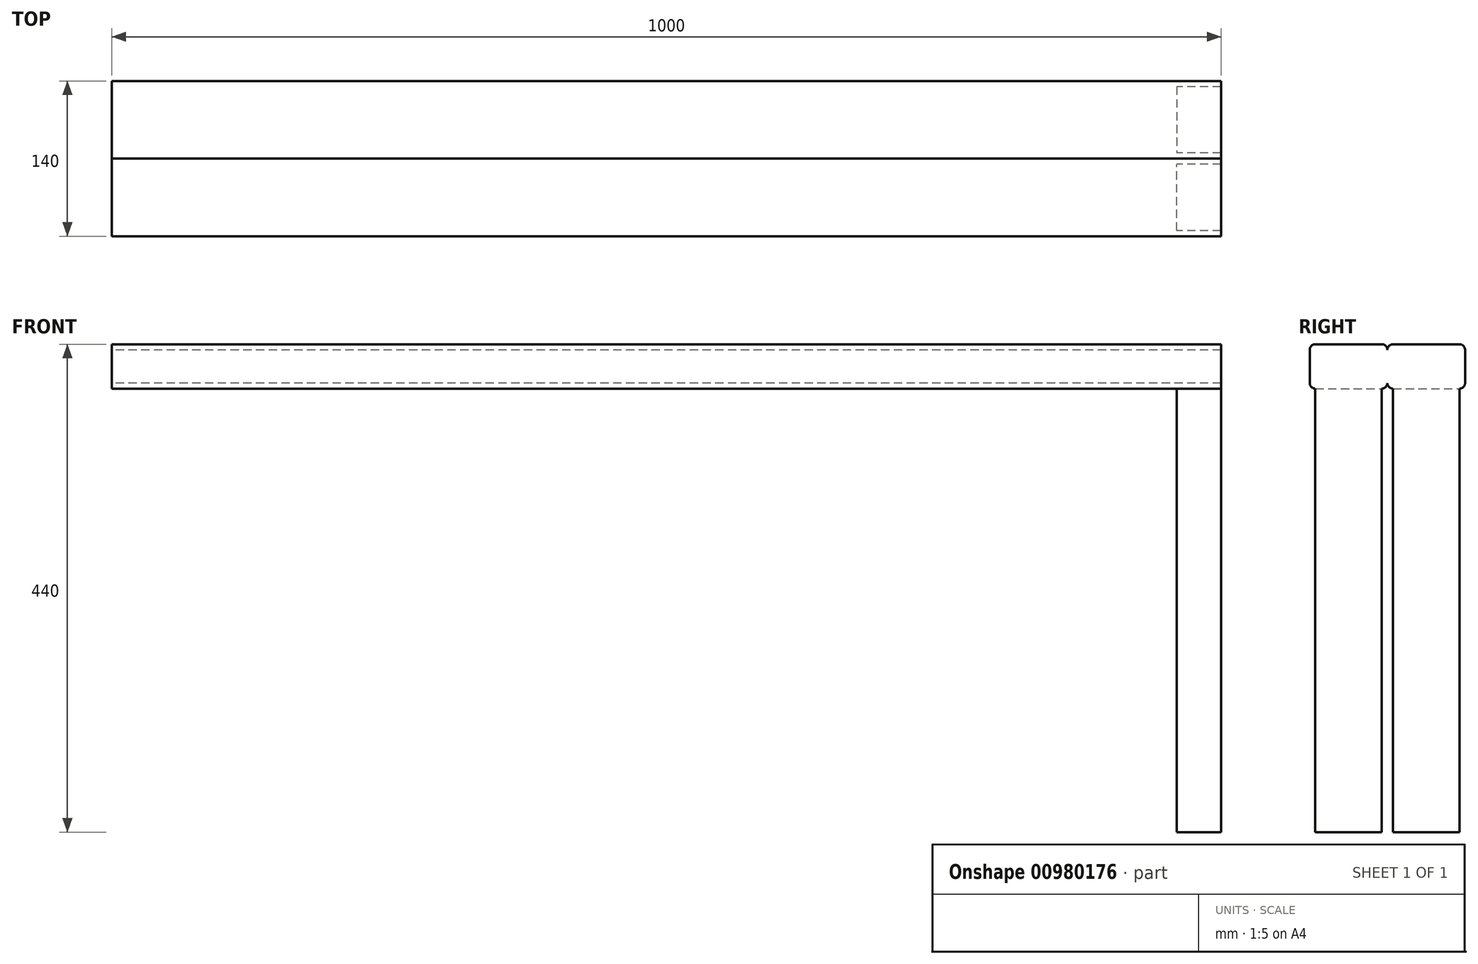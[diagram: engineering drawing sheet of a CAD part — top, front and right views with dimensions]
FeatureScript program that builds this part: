
annotation { "Feature Type Name" : "Feature", "Feature Type Description" : "" }
export const myFeature = defineFeature(function(context is Context, id is Id, definition is map)
    precondition{}
    {
        {
            var Q0;
            Q0=qCreatedBy(makeId("Right.planeOp"),FACE);
            var sketch = newSketch(context, id + "F0", { "sketchPlane" : qUnion([Q0])});
            skLineSegment(sketch, "E0.bottom", {"start": v(-5, 0) * mm, "end": v(-65, 0) * mm});
            skLineSegment(sketch, "E0.top", {"start": v(-5, 40) * mm, "end": v(-65, 40) * mm});
            skLineSegment(sketch, "E0.left", {"start": v(0, 5) * mm, "end": v(0, 35) * mm});
            skLineSegment(sketch, "E0.right", {"start": v(-70, 5) * mm, "end": v(-70, 35) * mm});
            skPoint(sketch, "E1.visualSharp", {"position": v(-70, 0) * mm});
            skArc(sketch, "E1.filletArc", {"start": v(-70, 5) * mm, "mid": v(-68.54, 1.46) * mm, "end": v(-65, 0) * mm});
            skPoint(sketch, "E2.visualSharp", {"position": v(0, 0) * mm});
            skArc(sketch, "E2.filletArc", {"start": v(-5, 0) * mm, "mid": v(-1.46, 1.46) * mm, "end": v(0, 5) * mm});
            skPoint(sketch, "E3.visualSharp", {"position": v(-70, 40) * mm});
            skArc(sketch, "E3.filletArc", {"start": v(-65, 40) * mm, "mid": v(-68.54, 38.54) * mm, "end": v(-70, 35) * mm});
            skPoint(sketch, "E4.visualSharp", {"position": v(0, 40) * mm});
            skArc(sketch, "E4.filletArc", {"start": v(0, 35) * mm, "mid": v(-1.46, 38.54) * mm, "end": v(-5, 40) * mm});
            skSolve(sketch);
        }
        {
            var Q0;
            Q0 = qSketchRegion(id + "F0", true);
            extrude(context, id + "F1", {"entities" : qUnion([Q0]), "endBound" : BoundingType.SYMMETRIC, "depth" : 1000 * mm, "offsetDistance" : 25 * mm});
        }
        {
            var Q0;
            Q0=makeQuery(id+"F1.opExtrude","SWEPT_FACE",FACE,{"disambiguationData":[OSD([sQuery(id+"F0.wireOp",EDGE,"E0.bottom")])]});
            var sketch = newSketch(context, id + "F2", { "sketchPlane" : qUnion([Q0])});
            skLineSegment(sketch, "E5.bottom", {"start": v(500, 65) * mm, "end": v(460, 65) * mm, "construction": true});
            skLineSegment(sketch, "E5.top", {"start": v(500, 5) * mm, "end": v(460, 5) * mm, "construction": true});
            skLineSegment(sketch, "E5.left", {"start": v(500, 65) * mm, "end": v(500, 5) * mm, "construction": true});
            skLineSegment(sketch, "E5.right", {"start": v(460, 65) * mm, "end": v(460, 5) * mm, "construction": true});
            skLineSegment(sketch, "E6.bottom", {"start": v(500, 65) * mm, "end": v(460, 65) * mm});
            skLineSegment(sketch, "E6.top", {"start": v(500, 5) * mm, "end": v(460, 5) * mm});
            skLineSegment(sketch, "E6.left", {"start": v(500, 65) * mm, "end": v(500, 5) * mm});
            skLineSegment(sketch, "E6.right", {"start": v(460, 65) * mm, "end": v(460, 5) * mm});
            skSolve(sketch);
        }
        {
            var Q0;
            Q0 = qSketchRegion(id + "F2", true);
            extrude(context, id + "F3", {"entities" : qUnion([Q0]), "operationType" : NewBodyOperationType.ADD, "depth" : 400 * mm, "offsetDistance" : 25 * mm});
        }
        {
            var Q0;
            Q0=makeQuery(id+"F1.opExtrude","SWEPT_BODY",BODY,{"disambiguationData":[OSD([sQuery(id+"F0.wireOp",EDGE,"E0.bottom"),sQuery(id+"F0.wireOp",EDGE,"E0.top"),sQuery(id+"F0.wireOp",EDGE,"E0.left"),sQuery(id+"F0.wireOp",EDGE,"E0.right"),sQuery(id+"F0.wireOp",EDGE,"E1.filletArc"),sQuery(id+"F0.wireOp",EDGE,"E2.filletArc"),sQuery(id+"F0.wireOp",EDGE,"E3.filletArc"),sQuery(id+"F0.wireOp",EDGE,"E4.filletArc")])]});
            var Q1;
            Q1=qCreatedBy(makeId("Front.planeOp"),FACE);
            mirror(context, id + "F4", {"operationType" : NewBodyOperationType.ADD, "entities" : qUnion([Q0]), "mirrorPlane" : qUnion([Q1])});
        }
    });
